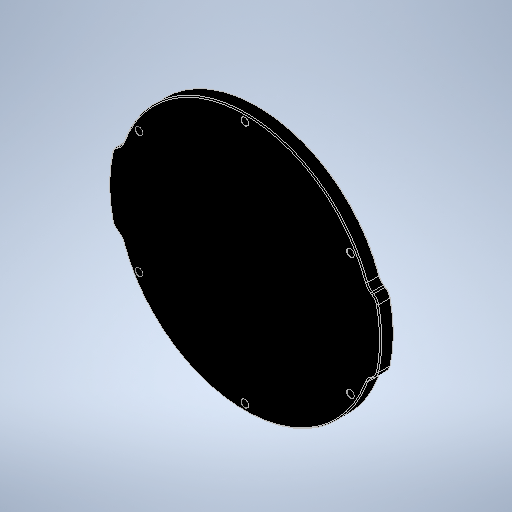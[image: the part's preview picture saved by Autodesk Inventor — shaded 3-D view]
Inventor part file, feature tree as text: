
AUTODESK INVENTOR PART (.ipt)
format: ipt  version: 2025.1 (Build 291241020, 241B)  size: 278,528 bytes
history: native  units: in
note: dims shown in document units (in); Inventor stores cm internally (conversion verified against a paired STEP export)
features: chamfer x1
ambient origin geometry x8: Origin, YZ Plane, XZ Plane, XY Plane, X Axis, Y Axis, Z Axis, Center Point
bodies: Solid1 (feature_tree)
feature tree (1):
  chamfer  "Chamfer21"  [1 undecoded]
note: 1 required parameter value undecoded (feature->parameter linkage not recoverable at this tier; creation-order binding heuristic only, values carry confidence <= 0.55)
